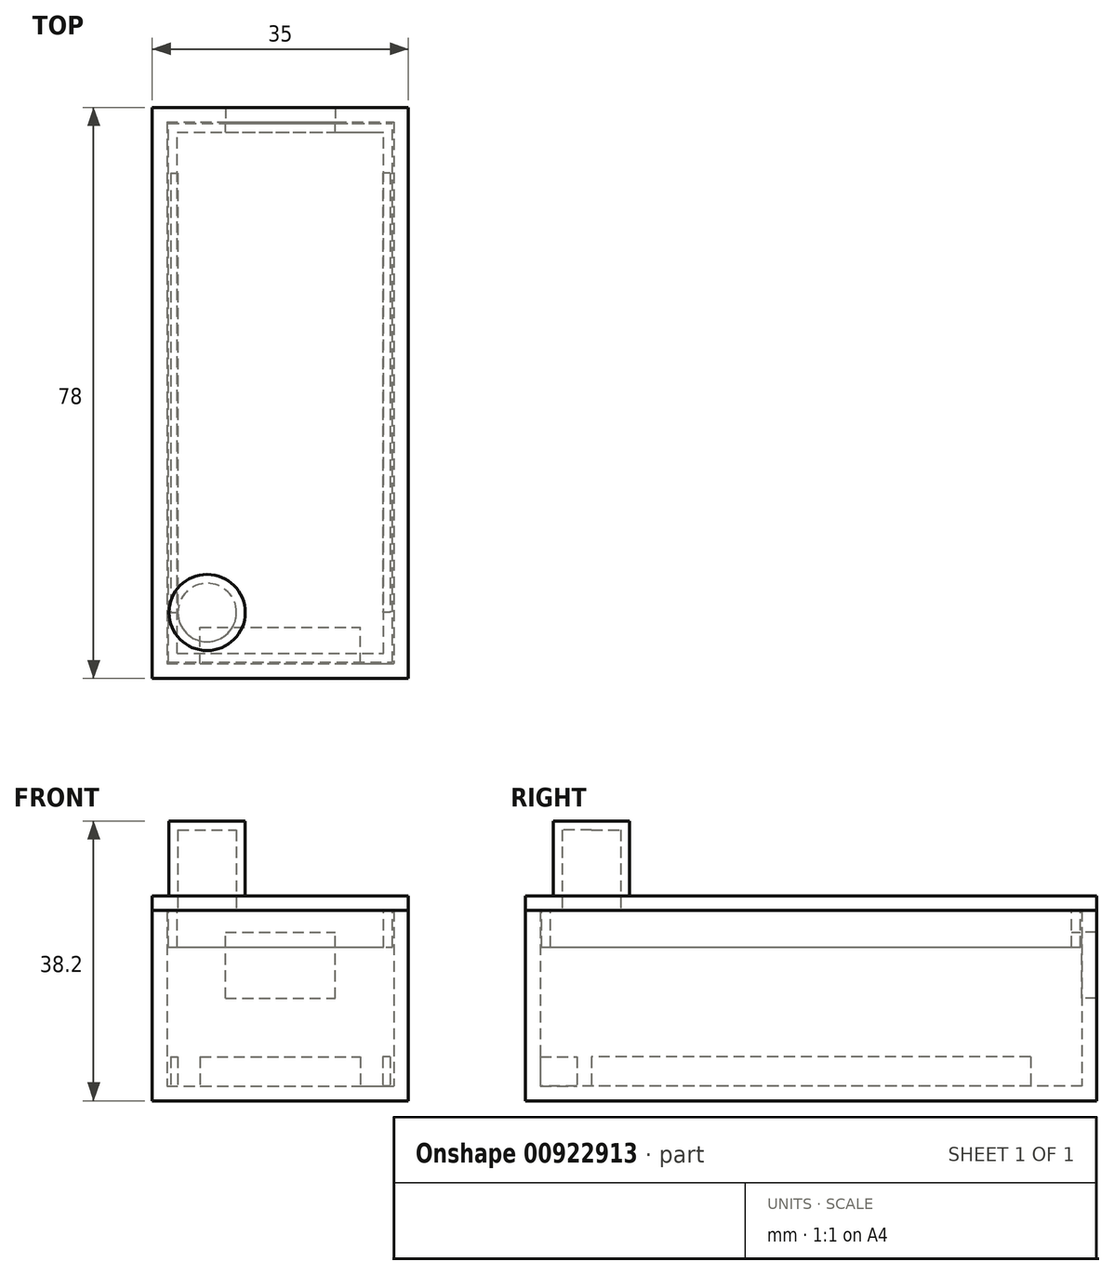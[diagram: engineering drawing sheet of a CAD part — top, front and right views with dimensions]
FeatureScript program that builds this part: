
annotation { "Feature Type Name" : "Feature", "Feature Type Description" : "" }
export const myFeature = defineFeature(function(context is Context, id is Id, definition is map)
    precondition{}
    {
        {
            var Q0;
            Q0=qCreatedBy(makeId("Top.planeOp"),FACE);
            var sketch = newSketch(context, id + "F0", { "sketchPlane" : qUnion([Q0])});
            skLineSegment(sketch, "E0.bottom", {"start": v(-17.5, 39) * mm, "end": v(17.5, 39) * mm});
            skLineSegment(sketch, "E0.top", {"start": v(-17.5, -39) * mm, "end": v(17.5, -39) * mm});
            skLineSegment(sketch, "E0.left", {"start": v(-17.5, 39) * mm, "end": v(-17.5, -39) * mm});
            skLineSegment(sketch, "E0.right", {"start": v(17.5, 39) * mm, "end": v(17.5, -39) * mm});
            skSolve(sketch);
        }
        {
            var Q0;
            Q0 = qSketchRegion(id + "F0", true);
            extrude(context, id + "F1", {"entities" : qUnion([Q0]), "depth" : 2 * mm, "offsetDistance" : 25 * mm});
        }
        {
            var Q0;
            Q0=makeQuery(id+"F1.opExtrude","CAP_FACE",FACE,{"disambiguationData":[OSD([sQuery(id+"F0.wireOp",EDGE,"E0.bottom"),sQuery(id+"F0.wireOp",EDGE,"E0.top"),sQuery(id+"F0.wireOp",EDGE,"E0.left"),sQuery(id+"F0.wireOp",EDGE,"E0.right")])],"isStart":false});
            var sketch = newSketch(context, id + "F2", { "sketchPlane" : qUnion([Q0])});
            skLineSegment(sketch, "E1.bottom", {"start": v(-15.5, 37) * mm, "end": v(15.5, 37) * mm});
            skLineSegment(sketch, "E1.top", {"start": v(-15.5, -37) * mm, "end": v(15.5, -37) * mm});
            skLineSegment(sketch, "E1.left", {"start": v(-15.5, 37) * mm, "end": v(-15.5, -37) * mm});
            skLineSegment(sketch, "E1.right", {"start": v(15.5, 37) * mm, "end": v(15.5, -37) * mm});
            skLineSegment(sketch, "E2.0", {"start": v(-17.5, 39) * mm, "end": v(-17.5, -39) * mm});
            skLineSegment(sketch, "E2.1", {"start": v(-17.5, 39) * mm, "end": v(17.5, 39) * mm});
            skLineSegment(sketch, "E2.2", {"start": v(17.5, 39) * mm, "end": v(17.5, -39) * mm});
            skLineSegment(sketch, "E2.3", {"start": v(-17.5, -39) * mm, "end": v(17.5, -39) * mm});
            skSolve(sketch);
        }
        {
            var Q0;
            Q0 = qSketchRegion(id + "F2", true);
            extrude(context, id + "F3", {"entities" : qUnion([Q0]), "operationType" : NewBodyOperationType.ADD, "depth" : 24 * mm, "offsetDistance" : 25 * mm});
        }
        {
            var Q0;
            Q0=makeQuery(id+"F1.opExtrude","CAP_FACE",FACE,{"disambiguationData":[OSD([sQuery(id+"F0.wireOp",EDGE,"E0.bottom"),sQuery(id+"F0.wireOp",EDGE,"E0.top"),sQuery(id+"F0.wireOp",EDGE,"E0.left"),sQuery(id+"F0.wireOp",EDGE,"E0.right")])],"isStart":false});
            var sketch = newSketch(context, id + "F4", { "sketchPlane" : qUnion([Q0])});
            skLineSegment(sketch, "E3.bottom", {"start": v(-15, 30) * mm, "end": v(15, 30) * mm, "construction": true});
            skLineSegment(sketch, "E3.top", {"start": v(-15, -30) * mm, "end": v(15, -30) * mm, "construction": true});
            skLineSegment(sketch, "E3.left", {"start": v(-15, 30) * mm, "end": v(-15, -30) * mm});
            skLineSegment(sketch, "E3.right", {"start": v(15, 30) * mm, "end": v(15, -30) * mm});
            skLineSegment(sketch, "E4.bottom", {"start": v(-15, 30) * mm, "end": v(-14, 30) * mm});
            skLineSegment(sketch, "E4.top", {"start": v(-15, -30) * mm, "end": v(-14, -30) * mm});
            skLineSegment(sketch, "E4.right", {"start": v(-14, 30) * mm, "end": v(-14, -30) * mm});
            skLineSegment(sketch, "E5.bottom", {"start": v(15, 30) * mm, "end": v(14, 30) * mm});
            skLineSegment(sketch, "E5.top", {"start": v(15, -30) * mm, "end": v(14, -30) * mm});
            skLineSegment(sketch, "E5.right", {"start": v(14, 30) * mm, "end": v(14, -30) * mm});
            skLineSegment(sketch, "E6.bottom", {"start": v(-10.96, -37) * mm, "end": v(10.96, -37) * mm});
            skLineSegment(sketch, "E6.top", {"start": v(-10.96, -32) * mm, "end": v(10.96, -32) * mm});
            skLineSegment(sketch, "E6.left", {"start": v(-10.96, -37) * mm, "end": v(-10.96, -32) * mm});
            skLineSegment(sketch, "E6.right", {"start": v(10.96, -37) * mm, "end": v(10.96, -32) * mm});
            skSolve(sketch);
        }
        {
            var Q0;
            Q0 = qSketchRegion(id + "F4", true);
            extrude(context, id + "F5", {"entities" : qUnion([Q0]), "operationType" : NewBodyOperationType.ADD, "depth" : 4 * mm, "offsetDistance" : 25 * mm});
        }
        {
            var Q0;
            Q0=makeQuery(id+"F3.opExtrude","SWEPT_FACE",FACE,{"disambiguationData":[OSD([sQuery(id+"F2.wireOp",EDGE,"E1.bottom")])]});
            var sketch = newSketch(context, id + "F6", { "sketchPlane" : qUnion([Q0])});
            skLineSegment(sketch, "E7.0", {"start": v(-15, 6) * mm, "end": v(-14, 6) * mm, "construction": true});
            skLineSegment(sketch, "E7.1", {"start": v(15, 6) * mm, "end": v(14, 6) * mm, "construction": true});
            skLineSegment(sketch, "E8", {"start": v(-14, 6) * mm, "end": v(14, 6) * mm, "construction": true});
            skLineSegment(sketch, "E9.bottom", {"start": v(-7.5, 14) * mm, "end": v(7.5, 14) * mm});
            skLineSegment(sketch, "E9.top", {"start": v(-7.5, 23) * mm, "end": v(7.5, 23) * mm});
            skLineSegment(sketch, "E9.left", {"start": v(-7.5, 14) * mm, "end": v(-7.5, 23) * mm});
            skLineSegment(sketch, "E9.right", {"start": v(7.5, 14) * mm, "end": v(7.5, 23) * mm});
            skSolve(sketch);
        }
        {
            var Q0;
            Q0 = qSketchRegion(id + "F6", true);
            extrude(context, id + "F7", {"entities" : qUnion([Q0]), "operationType" : NewBodyOperationType.REMOVE, "endBound" : BoundingType.UP_TO_NEXT, "oppositeDirection" : true, "depth" : 25 * mm, "offsetDistance" : 25 * mm});
        }
        {
            var Q0;
            Q0=makeQuery(id+"F3.opExtrude","CAP_FACE",FACE,{"disambiguationData":[OSD([sQuery(id+"F2.wireOp",EDGE,"E1.bottom"),sQuery(id+"F2.wireOp",EDGE,"E1.top"),sQuery(id+"F2.wireOp",EDGE,"E1.left"),sQuery(id+"F2.wireOp",EDGE,"E1.right"),sQuery(id+"F2.wireOp",EDGE,"E2.0"),sQuery(id+"F2.wireOp",EDGE,"E2.1"),sQuery(id+"F2.wireOp",EDGE,"E2.2"),sQuery(id+"F2.wireOp",EDGE,"E2.3")])],"isStart":false});
            var sketch = newSketch(context, id + "F8", { "sketchPlane" : qUnion([Q0])});
            skLineSegment(sketch, "E10.0", {"start": v(17.5, 39) * mm, "end": v(17.5, -39) * mm});
            skLineSegment(sketch, "E10.1", {"start": v(-17.5, -39) * mm, "end": v(17.5, -39) * mm});
            skLineSegment(sketch, "E10.2", {"start": v(-17.5, 39) * mm, "end": v(-17.5, -39) * mm});
            skLineSegment(sketch, "E10.3", {"start": v(-17.5, 39) * mm, "end": v(17.5, 39) * mm});
            skSolve(sketch);
        }
        {
            var Q0;
            Q0 = qSketchRegion(id + "F8", true);
            extrude(context, id + "F9", {"entities" : qUnion([Q0]), "depth" : 2 * mm, "offsetDistance" : 25 * mm});
        }
        {
            var Q0;
            Q0=makeQuery(id+"F9.opExtrude","CAP_FACE",FACE,{"disambiguationData":[OSD([sQuery(id+"F8.wireOp",EDGE,"E10.0"),sQuery(id+"F8.wireOp",EDGE,"E10.1"),sQuery(id+"F8.wireOp",EDGE,"E10.2"),sQuery(id+"F8.wireOp",EDGE,"E10.3")])],"isStart":true});
            var sketch = newSketch(context, id + "F10", { "sketchPlane" : qUnion([Q0])});
            skLineSegment(sketch, "E11.0", {"start": v(-15.5, 37) * mm, "end": v(15.5, 37) * mm, "construction": true});
            skLineSegment(sketch, "E11.1", {"start": v(15.5, -37) * mm, "end": v(15.5, 37) * mm, "construction": true});
            skLineSegment(sketch, "E11.2", {"start": v(-15.5, -37) * mm, "end": v(-15.5, 37) * mm, "construction": true});
            skLineSegment(sketch, "E11.3", {"start": v(-15.5, -37) * mm, "end": v(15.5, -37) * mm, "construction": true});
            skLineSegment(sketch, "E12.bottom", {"start": v(-15.3, 36.8) * mm, "end": v(15.3, 36.8) * mm});
            skLineSegment(sketch, "E12.top", {"start": v(-15.3, -36.8) * mm, "end": v(15.3, -36.8) * mm});
            skLineSegment(sketch, "E12.left", {"start": v(-15.3, 36.8) * mm, "end": v(-15.3, -36.8) * mm});
            skLineSegment(sketch, "E12.right", {"start": v(15.3, 36.8) * mm, "end": v(15.3, -36.8) * mm});
            skLineSegment(sketch, "E13.bottom", {"start": v(-14.1, 35.6) * mm, "end": v(14.1, 35.6) * mm});
            skLineSegment(sketch, "E13.top", {"start": v(-14.1, -35.6) * mm, "end": v(14.1, -35.6) * mm});
            skLineSegment(sketch, "E13.left", {"start": v(-14.1, 35.6) * mm, "end": v(-14.1, -35.6) * mm});
            skLineSegment(sketch, "E13.right", {"start": v(14.1, 35.6) * mm, "end": v(14.1, -35.6) * mm});
            skSolve(sketch);
        }
        {
            var Q0;
            Q0 = qSketchRegion(id + "F10", true);
            extrude(context, id + "F11", {"entities" : qUnion([Q0]), "operationType" : NewBodyOperationType.ADD, "depth" : 5 * mm, "offsetDistance" : 25 * mm});
        }
        {
            var Q0;
            Q0=makeQuery(id+"F9.opExtrude","CAP_FACE",FACE,{"disambiguationData":[OSD([sQuery(id+"F8.wireOp",EDGE,"E10.0"),sQuery(id+"F8.wireOp",EDGE,"E10.1"),sQuery(id+"F8.wireOp",EDGE,"E10.2"),sQuery(id+"F8.wireOp",EDGE,"E10.3")])],"isStart":false});
            var sketch = newSketch(context, id + "F12", { "sketchPlane" : qUnion([Q0])});
            skLineSegment(sketch, "E14.0", {"start": v(-15.5, 37) * mm, "end": v(-15.5, -37) * mm, "construction": true});
            skLineSegment(sketch, "E14.1", {"start": v(-15.5, 37) * mm, "end": v(15.5, 37) * mm, "construction": true});
            skLineSegment(sketch, "E14.2", {"start": v(15.5, 37) * mm, "end": v(15.5, -37) * mm, "construction": true});
            skLineSegment(sketch, "E14.3", {"start": v(-15.5, -37) * mm, "end": v(15.5, -37) * mm, "construction": true});
            skLineSegment(sketch, "E15.1", {"start": v(-17.5, 39) * mm, "end": v(-17.5, -39) * mm, "construction": true});
            skLineSegment(sketch, "E15.2", {"start": v(-17.5, 39) * mm, "end": v(17.5, 39) * mm, "construction": true});
            skLineSegment(sketch, "E15.3", {"start": v(17.5, 39) * mm, "end": v(17.5, -39) * mm, "construction": true});
            skLineSegment(sketch, "E15.4", {"start": v(-17.5, -39) * mm, "end": v(17.5, -39) * mm, "construction": true});
            skPoint(sketch, "E16", {"position": v(-10, -30) * mm});
            skCircle(sketch, "E17", {"center": v(-10, -30) * mm, "radius": 4 * mm});
            skCircle(sketch, "E18", {"center": v(-10, -30) * mm, "radius": 5.2 * mm});
            skLineSegment(sketch, "E19", {"start": v(-10, -30) * mm, "end": v(-10, -24.8) * mm, "construction": true});
            skPoint(sketch, "E20", {"position": v(-10, -26) * mm});
            skSolve(sketch);
        }
        {
            var Q0;
            Q0 = qSketchRegion(id + "F12", true);
            extrude(context, id + "F13", {"entities" : qUnion([Q0]), "operationType" : NewBodyOperationType.ADD, "depth" : 9 * mm, "offsetDistance" : 25 * mm});
        }
        {
            var Q0;
            Q0=makeQuery(id+"F13.opExtrude","CAP_FACE",FACE,{"disambiguationData":[OSD([sQuery(id+"F12.wireOp",EDGE,"E17"),sQuery(id+"F12.wireOp",EDGE,"E18")])],"isStart":false});
            var sketch = newSketch(context, id + "F14", { "sketchPlane" : qUnion([Q0])});
            skCircle(sketch, "E21.0", {"center": v(-10, -30) * mm, "radius": 5.2 * mm});
            skSolve(sketch);
        }
        {
            var Q0;
            Q0 = qSketchRegion(id + "F14", true);
            extrude(context, id + "F15", {"entities" : qUnion([Q0]), "operationType" : NewBodyOperationType.ADD, "depth" : 1.2 * mm, "offsetDistance" : 25 * mm});
        }
        {
            var Q0;
            Q0=makeQuery(id+"F11.boolean.opBoolean","SPLIT",FACE,{"disambiguationData":[TD([makeQuery(id+"F11.opExtrude","SWEPT_FACE",FACE,{"disambiguationData":[OSD([sQuery(id+"F10.wireOp",EDGE,"E13.bottom")])]})])],"derivedFrom":makeQuery(id+"F9.opExtrude","CAP_FACE",FACE,{"disambiguationData":[OSD([sQuery(id+"F8.wireOp",EDGE,"E10.0"),sQuery(id+"F8.wireOp",EDGE,"E10.1"),sQuery(id+"F8.wireOp",EDGE,"E10.2"),sQuery(id+"F8.wireOp",EDGE,"E10.3")])],"isStart":true})});
            var sketch = newSketch(context, id + "F16", { "sketchPlane" : qUnion([Q0])});
            skCircle(sketch, "E22.0", {"center": v(-10, 30) * mm, "radius": 4 * mm});
            skSolve(sketch);
        }
        {
            var Q0;
            Q0 = qSketchRegion(id + "F16", true);
            extrude(context, id + "F17", {"entities" : qUnion([Q0]), "operationType" : NewBodyOperationType.REMOVE, "endBound" : BoundingType.UP_TO_NEXT, "oppositeDirection" : true, "depth" : 25 * mm, "offsetDistance" : 25 * mm});
        }
        {
            var Q0;
            Q0=makeQuery(id+"F11.opExtrude","SWEPT_FACE",FACE,{"disambiguationData":[OSD([sQuery(id+"F10.wireOp",EDGE,"E12.top")])]});
            var sketch = newSketch(context, id + "F18", { "sketchPlane" : qUnion([Q0])});
            skLineSegment(sketch, "E23.0", {"start": v(7.5, 23) * mm, "end": v(-7.5, 23) * mm});
            skLineSegment(sketch, "E23.1", {"start": v(7.5, 14) * mm, "end": v(7.5, 23) * mm});
            skLineSegment(sketch, "E23.2", {"start": v(7.5, 14) * mm, "end": v(-7.5, 14) * mm});
            skLineSegment(sketch, "E23.3", {"start": v(-7.5, 14) * mm, "end": v(-7.5, 23) * mm});
            skSolve(sketch);
        }
        {
            var Q0;
            Q0 = qSketchRegion(id + "F18", true);
            var Q1;
            Q1=makeQuery(id+"F11.opExtrude","SWEPT_FACE",FACE,{"disambiguationData":[OSD([sQuery(id+"F10.wireOp",EDGE,"E13.top")])]});
            extrude(context, id + "F19", {"entities" : qUnion([Q0]), "operationType" : NewBodyOperationType.REMOVE, "endBound" : BoundingType.UP_TO_SURFACE, "oppositeDirection" : true, "depth" : 25 * mm, "endBoundEntityFace" : qUnion([Q1]), "offsetDistance" : 25 * mm});
        }
    });
